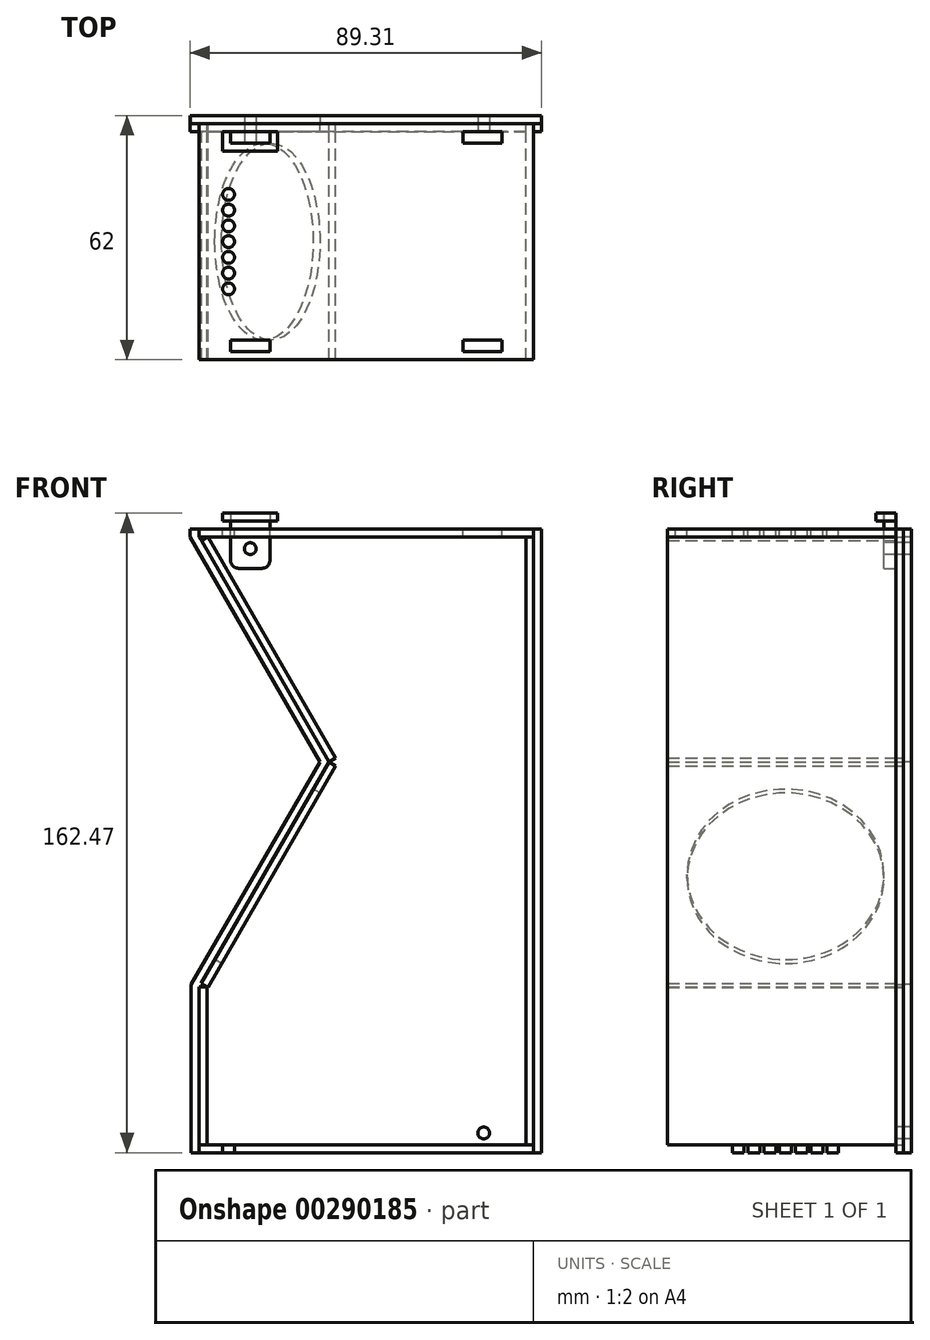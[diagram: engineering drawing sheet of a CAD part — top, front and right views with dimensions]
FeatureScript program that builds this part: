
annotation { "Feature Type Name" : "Feature", "Feature Type Description" : "" }
export const myFeature = defineFeature(function(context is Context, id is Id, definition is map)
    precondition{}
    {
        {
            assignVariable(context, id + "F0", {"name" : "pd", "anyValue" : 2});
        }
        {
            var Q0;
            Q0=qCreatedBy(makeId("Front.planeOp"),FACE);
            var sketch = newSketch(context, id + "F1", { "sketchPlane" : qUnion([Q0])});
            skLineSegment(sketch, "E0", {"start": v(0, 0) * mm, "end": v(25, 43.3) * mm});
            skLineSegment(sketch, "E1", {"start": v(0, 0) * mm, "end": v(43.3, -25) * mm, "construction": true});
            skLineSegment(sketch, "E2", {"start": v(25, 43.3) * mm, "end": v(68.3, 18.3) * mm, "construction": true});
            skLineSegment(sketch, "E3", {"start": v(43.3, -25) * mm, "end": v(68.3, 18.3) * mm, "construction": true});
            skLineSegment(sketch, "E4", {"start": v(0, 0) * mm, "end": v(-4, -6.93) * mm});
            skLineSegment(sketch, "E5", {"start": v(25, 43.3) * mm, "end": v(29, 50.23) * mm});
            skLineSegment(sketch, "E6", {"start": v(-4, 109.39) * mm, "end": v(81, 109.39) * mm});
            skLineSegment(sketch, "E7", {"start": v(81, 107.39) * mm, "end": v(-4, 107.39) * mm});
            skLineSegment(sketch, "E8", {"start": v(-4, 107.39) * mm, "end": v(-4, 109.39) * mm});
            skLineSegment(sketch, "E9", {"start": v(79, 107.39) * mm, "end": v(79, -47.08) * mm});
            skLineSegment(sketch, "E10", {"start": v(81, -49.08) * mm, "end": v(-4, -49.08) * mm});
            skLineSegment(sketch, "E11", {"start": v(-4, -49.08) * mm, "end": v(-4, -47.08) * mm});
            skLineSegment(sketch, "E12", {"start": v(-4, -6.93) * mm, "end": v(-4, -47.08) * mm});
            skLineSegment(sketch, "E13", {"start": v(-4, -6.93) * mm, "end": v(-2, -6.93) * mm});
            skLineSegment(sketch, "E14", {"start": v(-2, -6.93) * mm, "end": v(-2, -47.08) * mm});
            skLineSegment(sketch, "E15", {"start": v(29, 50.23) * mm, "end": v(-4, 107.39) * mm});
            skLineSegment(sketch, "E16", {"start": v(-3.5, -6.06) * mm, "end": v(-1.77, -7.06) * mm});
            skLineSegment(sketch, "E17", {"start": v(29, 50.23) * mm, "end": v(30.73, 49.23) * mm});
            skLineSegment(sketch, "E18", {"start": v(30.73, 49.23) * mm, "end": v(-1.77, -7.06) * mm});
            skLineSegment(sketch, "E19", {"start": v(29, 50.23) * mm, "end": v(30.73, 51.23) * mm});
            skLineSegment(sketch, "E20", {"start": v(30.73, 51.23) * mm, "end": v(-1.7, 107.39) * mm});
            skLineSegment(sketch, "E21", {"start": v(-1.7, 107.39) * mm, "end": v(-3.42, 106.39) * mm});
            skLineSegment(sketch, "E22", {"start": v(81, -49.08) * mm, "end": v(81, 109.39) * mm});
            skLineSegment(sketch, "E23", {"start": v(81, -47.08) * mm, "end": v(-4, -47.08) * mm});
            skSolve(sketch);
        }
        {
            var Q0;
            Q0=sQuery(id+"F1.wireOp",EDGE,"E0");
            cPlane(context, id + "F2", {"entities" : qUnion([Q0]), "cplaneType" : CPlaneType.LINE_ANGLE, "offset" : 25 * mm, "angle" : 0 * degree, "width" : 150 * mm, "height" : 150 * mm});
        }
        {
            var Q0;
            Q0=qCreatedBy(makeId("Front.planeOp"),FACE);
            cPlane(context, id + "F3", {"entities" : qUnion([Q0]), "cplaneType" : CPlaneType.OFFSET, "offset" : 30 * mm, "oppositeDirection" : true, "width" : 150 * mm, "height" : 150 * mm});
        }
        {
            var Q0;
            Q0=qCreatedBy(id+"F2.planeOp",FACE);
            var sketch = newSketch(context, id + "F4", { "sketchPlane" : qUnion([Q0])});
            skLineSegment(sketch, "E24.0", {"start": v(0, 0) * mm, "end": v(0, 50) * mm});
            skCircle(sketch, "E25", {"center": v(0, 25) * mm, "radius": 25 * mm});
            skLineSegment(sketch, "E26.bottom", {"start": v(30, -5) * mm, "end": v(-30, -5) * mm});
            skLineSegment(sketch, "E26.top", {"start": v(30, 55) * mm, "end": v(-30, 55) * mm});
            skLineSegment(sketch, "E26.left", {"start": v(30, -5) * mm, "end": v(30, 55) * mm});
            skLineSegment(sketch, "E26.right", {"start": v(-30, -5) * mm, "end": v(-30, 55) * mm});
            skSolve(sketch);
        }
        {
            var Q0;
            Q0=qCreatedBy(id+"F3.planeOp",FACE);
            var sketch = newSketch(context, id + "F5", { "sketchPlane" : qUnion([Q0])});
            skLineSegment(sketch, "E27.0.0", {"start": v(-2, -47.08) * mm, "end": v(79, -47.08) * mm});
            skLineSegment(sketch, "E27.0.1", {"start": v(79, -47.08) * mm, "end": v(79, 107.39) * mm});
            skLineSegment(sketch, "E27.0.2", {"start": v(79, 107.39) * mm, "end": v(-1.7, 107.39) * mm});
            skLineSegment(sketch, "E27.0.3", {"start": v(-1.7, 107.39) * mm, "end": v(30.73, 51.23) * mm});
            skLineSegment(sketch, "E27.0.4", {"start": v(30.73, 51.23) * mm, "end": v(29, 50.23) * mm});
            skLineSegment(sketch, "E27.0.5", {"start": v(29, 50.23) * mm, "end": v(30.73, 49.23) * mm});
            skLineSegment(sketch, "E27.0.6", {"start": v(30.73, 49.23) * mm, "end": v(-1.77, -7.06) * mm});
            skLineSegment(sketch, "E27.0.7", {"start": v(-1.77, -7.06) * mm, "end": v(-2, -6.93) * mm});
            skLineSegment(sketch, "E27.0.8", {"start": v(-2, -6.93) * mm, "end": v(-2, -47.08) * mm});
            skLineSegment(sketch, "E28.0", {"start": v(-4, 109.39) * mm, "end": v(81, 109.39) * mm});
            skLineSegment(sketch, "E28.1", {"start": v(-4, 107.39) * mm, "end": v(-4, 109.39) * mm});
            skLineSegment(sketch, "E28.2", {"start": v(29, 50.23) * mm, "end": v(-4, 107.39) * mm});
            skLineSegment(sketch, "E28.3", {"start": v(81, -49.08) * mm, "end": v(81, 109.39) * mm});
            skLineSegment(sketch, "E28.4", {"start": v(25, 43.3) * mm, "end": v(29, 50.23) * mm});
            skLineSegment(sketch, "E28.5", {"start": v(0, 0) * mm, "end": v(25, 43.3) * mm});
            skLineSegment(sketch, "E28.6", {"start": v(0, 0) * mm, "end": v(-4, -6.93) * mm});
            skLineSegment(sketch, "E28.7", {"start": v(-4, -6.93) * mm, "end": v(-4, -47.08) * mm});
            skLineSegment(sketch, "E28.8", {"start": v(-4, -49.08) * mm, "end": v(-4, -47.08) * mm});
            skLineSegment(sketch, "E28.9", {"start": v(81, -49.08) * mm, "end": v(-4, -49.08) * mm});
            skLineSegment(sketch, "E29", {"start": v(-4, -49.08) * mm, "end": v(-6, -49.08) * mm});
            skLineSegment(sketch, "E30", {"start": v(-6, -49.08) * mm, "end": v(-6, -6.4) * mm});
            skLineSegment(sketch, "E31", {"start": v(-6, -6.4) * mm, "end": v(26.7, 50.23) * mm});
            skLineSegment(sketch, "E32", {"start": v(26.7, 50.23) * mm, "end": v(-6.3, 107.39) * mm});
            skLineSegment(sketch, "E33", {"start": v(-6.3, 107.39) * mm, "end": v(-6.3, 109.39) * mm});
            skLineSegment(sketch, "E34", {"start": v(-6.3, 109.39) * mm, "end": v(-4, 109.39) * mm});
            skLineSegment(sketch, "E35", {"start": v(81, -49.08) * mm, "end": v(83, -49.08) * mm});
            skLineSegment(sketch, "E36", {"start": v(83, -49.08) * mm, "end": v(83, 109.39) * mm});
            skLineSegment(sketch, "E37", {"start": v(83, 109.39) * mm, "end": v(81, 109.39) * mm});
            skSolve(sketch);
        }
        {
            var Q0;
            Q0=qCreatedBy(id+"F3.planeOp",FACE);
            var sketch = newSketch(context, id + "F6", { "sketchPlane" : qUnion([Q0])});
            skLineSegment(sketch, "E38.0", {"start": v(81, -49.08) * mm, "end": v(-4, -49.08) * mm});
            skLineSegment(sketch, "E38.1", {"start": v(-4, -49.08) * mm, "end": v(-6, -49.08) * mm});
            skLineSegment(sketch, "E38.2", {"start": v(-6, -49.08) * mm, "end": v(-6, -6.4) * mm});
            skLineSegment(sketch, "E38.3", {"start": v(-6, -6.4) * mm, "end": v(26.7, 50.23) * mm});
            skLineSegment(sketch, "E38.4", {"start": v(26.7, 50.23) * mm, "end": v(-6.3, 107.39) * mm});
            skLineSegment(sketch, "E38.5", {"start": v(-6.3, 107.39) * mm, "end": v(-6.3, 109.39) * mm});
            skLineSegment(sketch, "E38.6", {"start": v(-6.3, 109.39) * mm, "end": v(-4, 109.39) * mm});
            skLineSegment(sketch, "E38.7", {"start": v(-4, 109.39) * mm, "end": v(81, 109.39) * mm});
            skLineSegment(sketch, "E38.8", {"start": v(83, -49.08) * mm, "end": v(83, 109.39) * mm});
            skLineSegment(sketch, "E38.9", {"start": v(83, 109.39) * mm, "end": v(81, 109.39) * mm});
            skLineSegment(sketch, "E38.10", {"start": v(81, -49.08) * mm, "end": v(83, -49.08) * mm});
            skSolve(sketch);
        }
        {
            var Q0;
            {var subQ6=sQuery(id+"F1.wireOp",EDGE,"E6");Q0=makeQuery(id+"F1.imprint","IMPRINT",FACE,{"disambiguationData":[TD([[makeQuery(id+"F1.imprint","IMPRINT",EDGE,{"derivedFrom":subQ6}),-1.0]])]});}
            extrude(context, id + "F7", {"entities" : qUnion([Q0]), "depth" : 30 * mm, "hasSecondDirection" : true, "secondDirectionOppositeDirection" : true, "secondDirectionDepth" : 30 * mm});
        }
        {
            var Q0;
            {var subQ3=sQuery(id+"F1.wireOp",EDGE,"E9");Q0=makeQuery(id+"F1.imprint","IMPRINT",FACE,{"disambiguationData":[TD([[makeQuery(id+"F1.imprint","IMPRINT",EDGE,{"derivedFrom":subQ3}),1.0]])]});}
            extrude(context, id + "F8", {"entities" : qUnion([Q0]), "depth" : 30 * mm, "hasSecondDirection" : true, "secondDirectionOppositeDirection" : true, "secondDirectionDepth" : 30 * mm});
        }
        {
            var Q0;
            {var subQ0=sQuery(id+"F1.wireOp",EDGE,"E19");Q0=makeQuery(id+"F1.imprint","IMPRINT",FACE,{"disambiguationData":[TD([[makeQuery(id+"F1.imprint","IMPRINT",EDGE,{"derivedFrom":subQ0}),1.0]])]});}
            extrude(context, id + "F9", {"entities" : qUnion([Q0]), "depth" : 30 * mm, "hasSecondDirection" : true, "secondDirectionOppositeDirection" : true, "secondDirectionDepth" : 30 * mm});
        }
        {
            var Q0;
            {var subQ4=sQuery(id+"F1.wireOp",EDGE,"E0");Q0=makeQuery(id+"F1.imprint","IMPRINT",FACE,{"disambiguationData":[TD([[makeQuery(id+"F1.imprint","IMPRINT",EDGE,{"derivedFrom":subQ4}),-1.0]])]});}
            extrude(context, id + "F10", {"entities" : qUnion([Q0]), "depth" : 30 * mm, "hasSecondDirection" : true, "secondDirectionOppositeDirection" : true, "secondDirectionDepth" : 30 * mm});
        }
        {
            var Q0;
            {var subQ0=sQuery(id+"F1.wireOp",EDGE,"E12");Q0=makeQuery(id+"F1.imprint","IMPRINT",FACE,{"disambiguationData":[TD([[makeQuery(id+"F1.imprint","IMPRINT",EDGE,{"derivedFrom":subQ0}),1.0]])]});}
            extrude(context, id + "F11", {"entities" : qUnion([Q0]), "depth" : 30 * mm, "hasSecondDirection" : true, "secondDirectionOppositeDirection" : true, "secondDirectionDepth" : 30 * mm});
        }
        {
            var Q0;
            {var subQ4=sQuery(id+"F1.wireOp",EDGE,"E10");Q0=makeQuery(id+"F1.imprint","IMPRINT",FACE,{"disambiguationData":[TD([[makeQuery(id+"F1.imprint","IMPRINT",EDGE,{"derivedFrom":subQ4}),-1.0]])]});}
            extrude(context, id + "F12", {"entities" : qUnion([Q0]), "depth" : 30 * mm, "hasSecondDirection" : true, "secondDirectionOppositeDirection" : true, "secondDirectionDepth" : 30 * mm});
        }
        {
            var Q0;
            {var subQ0=sQuery(id+"F4.wireOp",EDGE,"E24.0");Q0=makeQuery(id+"F4.imprint","IMPRINT",FACE,{"disambiguationData":[TD([[makeQuery(id+"F4.imprint","IMPRINT",EDGE,{"derivedFrom":subQ0}),-1.0]])]});}
            var Q1;
            {var subQ0=sQuery(id+"F4.wireOp",EDGE,"E24.0");Q1=makeQuery(id+"F4.imprint","IMPRINT",FACE,{"disambiguationData":[TD([[makeQuery(id+"F4.imprint","IMPRINT",EDGE,{"derivedFrom":subQ0}),1.0]])]});}
            extrude(context, id + "F13", {"entities" : qUnion([Q0, Q1]), "operationType" : NewBodyOperationType.REMOVE, "depth" : 25 * mm});
        }
        {
            var Q0;
            Q0=makeQuery(id+"F7.opExtrude","SWEPT_FACE",FACE,{"disambiguationData":[OSD([sQuery(id+"F1.wireOp",EDGE,"E6")])]});
            var sketch = newSketch(context, id + "F14", { "sketchPlane" : qUnion([Q0])});
            skLineSegment(sketch, "E39", {"start": v(3.5, 30) * mm, "end": v(3.5, -30) * mm, "construction": true});
            skCircle(sketch, "E40", {"center": v(3.5, -12) * mm, "radius": 1.5 * mm});
            skCircle(sketch, "E41.0.1.0", {"center": v(3.5, -8) * mm, "radius": 1.5 * mm});
            skCircle(sketch, "E41.0.2.0", {"center": v(3.5, -4) * mm, "radius": 1.5 * mm});
            skCircle(sketch, "E41.0.3.0", {"center": v(3.5, 0) * mm, "radius": 1.5 * mm});
            skCircle(sketch, "E41.0.4.0", {"center": v(3.5, 4) * mm, "radius": 1.5 * mm});
            skCircle(sketch, "E41.0.5.0", {"center": v(3.5, 8) * mm, "radius": 1.5 * mm});
            skCircle(sketch, "E41.0.6.0", {"center": v(3.5, 12) * mm, "radius": 1.5 * mm});
            skLineSegment(sketch, "E41.direction1", {"start": v(3.5, -12) * mm, "end": v(64.86, -12) * mm, "construction": true});
            skLineSegment(sketch, "E41.direction2", {"start": v(3.5, -12) * mm, "end": v(3.5, -8) * mm, "construction": true});
            skLineSegment(sketch, "E42.bottom", {"start": v(14, 28) * mm, "end": v(4, 28) * mm});
            skLineSegment(sketch, "E42.top", {"start": v(14, 25) * mm, "end": v(4, 25) * mm});
            skLineSegment(sketch, "E42.left", {"start": v(14, 25) * mm, "end": v(14, 28) * mm});
            skLineSegment(sketch, "E42.right", {"start": v(4, 25) * mm, "end": v(4, 28) * mm});
            skPoint(sketch, "E42.middle", {"position": v(9, 26.5) * mm});
            skLineSegment(sketch, "E43", {"start": v(38.5, -30) * mm, "end": v(38.5, 30) * mm, "construction": true});
            skLineSegment(sketch, "E44.MirrorCS", {"start": v(63, 25) * mm, "end": v(73, 25) * mm});
            skLineSegment(sketch, "E45.MirrorCS", {"start": v(63, 28) * mm, "end": v(73, 28) * mm});
            skLineSegment(sketch, "E46.MirrorCS", {"start": v(73, 25) * mm, "end": v(73, 28) * mm});
            skLineSegment(sketch, "E47.MirrorCS", {"start": v(63, 25) * mm, "end": v(63, 28) * mm});
            skLineSegment(sketch, "E48.MirrorCS", {"start": v(14, -25) * mm, "end": v(4, -25) * mm});
            skLineSegment(sketch, "E49.MirrorCS", {"start": v(14, -25) * mm, "end": v(14, -28) * mm});
            skLineSegment(sketch, "E50.MirrorCS", {"start": v(14, -28) * mm, "end": v(4, -28) * mm});
            skLineSegment(sketch, "E51.MirrorCS", {"start": v(4, -25) * mm, "end": v(4, -28) * mm});
            skLineSegment(sketch, "E52.MirrorCS", {"start": v(63, -25) * mm, "end": v(63, -28) * mm});
            skLineSegment(sketch, "E53.MirrorCS", {"start": v(63, -28) * mm, "end": v(73, -28) * mm});
            skLineSegment(sketch, "E54.MirrorCS", {"start": v(73, -25) * mm, "end": v(73, -28) * mm});
            skLineSegment(sketch, "E55.MirrorCS", {"start": v(63, -25) * mm, "end": v(73, -25) * mm});
            skSolve(sketch);
        }
        {
            var Q0;
            Q0=makeQuery(id+"F14.imprint","IMPRINT",FACE,{"disambiguationData":[TD([[makeQuery(id+"F14.imprint","IMPRINT",EDGE,{"derivedFrom":sQuery(id+"F14.wireOp",EDGE,"E41.0.8.0")}),1.0]])]});
            var Q1;
            Q1=makeQuery(id+"F14.imprint","IMPRINT",FACE,{"disambiguationData":[TD([[makeQuery(id+"F14.imprint","IMPRINT",EDGE,{"derivedFrom":sQuery(id+"F14.wireOp",EDGE,"E41.0.7.0")}),1.0]])]});
            var Q2;
            Q2=makeQuery(id+"F14.imprint","IMPRINT",FACE,{"disambiguationData":[TD([[makeQuery(id+"F14.imprint","IMPRINT",EDGE,{"derivedFrom":sQuery(id+"F14.wireOp",EDGE,"E41.0.6.0")}),1.0]])]});
            var Q3;
            Q3=makeQuery(id+"F14.imprint","IMPRINT",FACE,{"disambiguationData":[TD([[makeQuery(id+"F14.imprint","IMPRINT",EDGE,{"derivedFrom":sQuery(id+"F14.wireOp",EDGE,"E41.0.5.0")}),1.0]])]});
            var Q4;
            Q4=makeQuery(id+"F14.imprint","IMPRINT",FACE,{"disambiguationData":[TD([[makeQuery(id+"F14.imprint","IMPRINT",EDGE,{"derivedFrom":sQuery(id+"F14.wireOp",EDGE,"E41.0.4.0")}),1.0]])]});
            var Q5;
            Q5=makeQuery(id+"F14.imprint","IMPRINT",FACE,{"disambiguationData":[TD([[makeQuery(id+"F14.imprint","IMPRINT",EDGE,{"derivedFrom":sQuery(id+"F14.wireOp",EDGE,"E41.0.2.0")}),1.0]])]});
            var Q6;
            Q6=makeQuery(id+"F14.imprint","IMPRINT",FACE,{"disambiguationData":[TD([[makeQuery(id+"F14.imprint","IMPRINT",EDGE,{"derivedFrom":sQuery(id+"F14.wireOp",EDGE,"E41.0.3.0")}),1.0]])]});
            var Q7;
            Q7=makeQuery(id+"F14.imprint","IMPRINT",FACE,{"disambiguationData":[TD([[makeQuery(id+"F14.imprint","IMPRINT",EDGE,{"derivedFrom":sQuery(id+"F14.wireOp",EDGE,"E41.0.1.0")}),1.0]])]});
            var Q8;
            Q8=makeQuery(id+"F14.imprint","IMPRINT",FACE,{"disambiguationData":[TD([[makeQuery(id+"F14.imprint","IMPRINT",EDGE,{"derivedFrom":sQuery(id+"F14.wireOp",EDGE,"E40")}),1.0]])]});
            var Q9;
            Q9=makeQuery(id+"F14.imprint","IMPRINT",FACE,{"disambiguationData":[TD([[makeQuery(id+"F14.imprint","IMPRINT",EDGE,{"derivedFrom":sQuery(id+"F14.wireOp",EDGE,"E42.bottom")}),1.0]])]});
            var Q10;
            Q10=makeQuery(id+"F14.imprint","IMPRINT",FACE,{"disambiguationData":[TD([[makeQuery(id+"F14.imprint","IMPRINT",EDGE,{"derivedFrom":sQuery(id+"F14.wireOp",EDGE,"E44.MirrorCS")}),1.0]])]});
            var Q11;
            Q11=makeQuery(id+"F14.imprint","IMPRINT",FACE,{"disambiguationData":[TD([[makeQuery(id+"F14.imprint","IMPRINT",EDGE,{"derivedFrom":sQuery(id+"F14.wireOp",EDGE,"E52.MirrorCS")}),1.0]])]});
            var Q12;
            Q12=makeQuery(id+"F14.imprint","IMPRINT",FACE,{"disambiguationData":[TD([[makeQuery(id+"F14.imprint","IMPRINT",EDGE,{"derivedFrom":sQuery(id+"F14.wireOp",EDGE,"E48.MirrorCS")}),1.0]])]});
            extrude(context, id + "F15", {"entities" : qUnion([Q0, Q1, Q2, Q3, Q4, Q5, Q6, Q7, Q8, Q9, Q10, Q11, Q12]), "operationType" : NewBodyOperationType.REMOVE, "oppositeDirection" : true, "depth" : (getVariable(context, 'pd')) * mm});
        }
        {
            var Q0;
            Q0=makeQuery(id+"F12.opExtrude","SWEPT_FACE",FACE,{"disambiguationData":[OSD([sQuery(id+"F1.wireOp",EDGE,"E10")])]});
            var sketch = newSketch(context, id + "F16", { "sketchPlane" : qUnion([Q0])});
            skLineSegment(sketch, "E56.0", {"start": v(14, 25) * mm, "end": v(4, 25) * mm});
            skLineSegment(sketch, "E56.1", {"start": v(14, 28) * mm, "end": v(4, 28) * mm});
            skLineSegment(sketch, "E56.2", {"start": v(14, 25) * mm, "end": v(14, 28) * mm});
            skLineSegment(sketch, "E56.3", {"start": v(4, 25) * mm, "end": v(4, 28) * mm});
            skCircle(sketch, "E56.4", {"center": v(3.5, 12) * mm, "radius": 1.5 * mm});
            skCircle(sketch, "E56.5", {"center": v(3.5, 8) * mm, "radius": 1.5 * mm});
            skCircle(sketch, "E56.6", {"center": v(3.5, 4) * mm, "radius": 1.5 * mm});
            skCircle(sketch, "E56.7", {"center": v(3.5, 0) * mm, "radius": 1.5 * mm});
            skCircle(sketch, "E56.8", {"center": v(3.5, -4) * mm, "radius": 1.5 * mm});
            skCircle(sketch, "E56.9", {"center": v(3.5, -8) * mm, "radius": 1.5 * mm});
            skCircle(sketch, "E56.10", {"center": v(3.5, -12) * mm, "radius": 1.5 * mm});
            skLineSegment(sketch, "E56.11", {"start": v(14, -25) * mm, "end": v(4, -25) * mm});
            skLineSegment(sketch, "E56.12", {"start": v(14, -28) * mm, "end": v(4, -28) * mm});
            skLineSegment(sketch, "E56.13", {"start": v(14, -25) * mm, "end": v(14, -28) * mm});
            skLineSegment(sketch, "E56.14", {"start": v(4, -25) * mm, "end": v(4, -28) * mm});
            skLineSegment(sketch, "E56.15", {"start": v(63, -25) * mm, "end": v(73, -25) * mm});
            skLineSegment(sketch, "E56.16", {"start": v(63, -28) * mm, "end": v(73, -28) * mm});
            skLineSegment(sketch, "E56.17", {"start": v(73, -25) * mm, "end": v(73, -28) * mm});
            skLineSegment(sketch, "E56.18", {"start": v(63, -25) * mm, "end": v(63, -28) * mm});
            skLineSegment(sketch, "E56.19", {"start": v(63, 25) * mm, "end": v(73, 25) * mm});
            skLineSegment(sketch, "E56.20", {"start": v(63, 25) * mm, "end": v(63, 28) * mm});
            skLineSegment(sketch, "E56.21", {"start": v(63, 28) * mm, "end": v(73, 28) * mm});
            skLineSegment(sketch, "E56.22", {"start": v(73, 25) * mm, "end": v(73, 28) * mm});
            skSolve(sketch);
        }
        {
            var Q0;
            Q0=makeQuery(id+"F16.imprint","IMPRINT",FACE,{"disambiguationData":[TD([[makeQuery(id+"F16.imprint","IMPRINT",EDGE,{"derivedFrom":sQuery(id+"F16.wireOp",EDGE,"E56.11")}),1.0]])]});
            var Q1;
            Q1=makeQuery(id+"F16.imprint","IMPRINT",FACE,{"disambiguationData":[TD([[makeQuery(id+"F16.imprint","IMPRINT",EDGE,{"derivedFrom":sQuery(id+"F16.wireOp",EDGE,"E56.10")}),-1.0]])]});
            var Q2;
            Q2=makeQuery(id+"F16.imprint","IMPRINT",FACE,{"disambiguationData":[TD([[makeQuery(id+"F16.imprint","IMPRINT",EDGE,{"derivedFrom":sQuery(id+"F16.wireOp",EDGE,"E56.9")}),-1.0]])]});
            var Q3;
            Q3=makeQuery(id+"F16.imprint","IMPRINT",FACE,{"disambiguationData":[TD([[makeQuery(id+"F16.imprint","IMPRINT",EDGE,{"derivedFrom":sQuery(id+"F16.wireOp",EDGE,"E56.8")}),-1.0]])]});
            var Q4;
            Q4=makeQuery(id+"F16.imprint","IMPRINT",FACE,{"disambiguationData":[TD([[makeQuery(id+"F16.imprint","IMPRINT",EDGE,{"derivedFrom":sQuery(id+"F16.wireOp",EDGE,"E56.7")}),-1.0]])]});
            var Q5;
            Q5=makeQuery(id+"F16.imprint","IMPRINT",FACE,{"disambiguationData":[TD([[makeQuery(id+"F16.imprint","IMPRINT",EDGE,{"derivedFrom":sQuery(id+"F16.wireOp",EDGE,"E56.6")}),-1.0]])]});
            var Q6;
            Q6=makeQuery(id+"F16.imprint","IMPRINT",FACE,{"disambiguationData":[TD([[makeQuery(id+"F16.imprint","IMPRINT",EDGE,{"derivedFrom":sQuery(id+"F16.wireOp",EDGE,"E56.5")}),-1.0]])]});
            var Q7;
            Q7=makeQuery(id+"F16.imprint","IMPRINT",FACE,{"disambiguationData":[TD([[makeQuery(id+"F16.imprint","IMPRINT",EDGE,{"derivedFrom":sQuery(id+"F16.wireOp",EDGE,"E56.4")}),-1.0]])]});
            var Q8;
            Q8=makeQuery(id+"F16.imprint","IMPRINT",FACE,{"disambiguationData":[TD([[makeQuery(id+"F16.imprint","IMPRINT",EDGE,{"derivedFrom":sQuery(id+"F16.wireOp",EDGE,"E56.0")}),-1.0]])]});
            var Q9;
            Q9=makeQuery(id+"F16.imprint","IMPRINT",FACE,{"disambiguationData":[TD([[makeQuery(id+"F16.imprint","IMPRINT",EDGE,{"derivedFrom":sQuery(id+"F16.wireOp",EDGE,"E56.19")}),1.0]])]});
            var Q10;
            Q10=makeQuery(id+"F16.imprint","IMPRINT",FACE,{"disambiguationData":[TD([[makeQuery(id+"F16.imprint","IMPRINT",EDGE,{"derivedFrom":sQuery(id+"F16.wireOp",EDGE,"E56.15")}),-1.0]])]});
            extrude(context, id + "F17", {"entities" : qUnion([Q0, Q1, Q2, Q3, Q4, Q5, Q6, Q7, Q8, Q9, Q10]), "operationType" : NewBodyOperationType.REMOVE, "oppositeDirection" : true, "depth" : (getVariable(context, 'pd')) * mm});
        }
        {
            var Q0;
            Q0=makeQuery(id+"F5.imprint","IMPRINT",FACE,{"disambiguationData":[TD([[makeQuery(id+"F5.imprint","IMPRINT",EDGE,{"derivedFrom":sQuery(id+"F5.wireOp",EDGE,"E27.0.0")}),1.0]])]});
            extrude(context, id + "F18", {"entities" : qUnion([Q0]), "depth" : (getVariable(context, 'pd')) * mm});
        }
        {
            var Q0;
            Q0=makeQuery(id+"F5.imprint","IMPRINT",FACE,{"disambiguationData":[TD([[makeQuery(id+"F5.imprint","IMPRINT",EDGE,{"derivedFrom":sQuery(id+"F5.wireOp",EDGE,"E28.3")}),-1.0]])]});
            var Q1;
            Q1=makeQuery(id+"F5.imprint","IMPRINT",FACE,{"disambiguationData":[TD([[makeQuery(id+"F5.imprint","IMPRINT",EDGE,{"derivedFrom":sQuery(id+"F5.wireOp",EDGE,"E28.1")}),1.0]])]});
            extrude(context, id + "F19", {"entities" : qUnion([Q0, Q1]), "depth" : (getVariable(context, 'pd')) * mm});
        }
        {
            var Q0;
            Q0=makeQuery(id+"F6.imprint","IMPRINT",FACE,{"disambiguationData":[TD([[makeQuery(id+"F6.imprint","IMPRINT",EDGE,{"derivedFrom":sQuery(id+"F6.wireOp",EDGE,"E38.0")}),-1.0]])]});
            extrude(context, id + "F20", {"entities" : qUnion([Q0]), "oppositeDirection" : true, "depth" : (getVariable(context, 'pd')) * mm});
        }
        {
            var Q0;
            Q0=makeQuery(id+"F14.imprint","IMPRINT",FACE,{"disambiguationData":[TD([[makeQuery(id+"F14.imprint","IMPRINT",EDGE,{"derivedFrom":sQuery(id+"F14.wireOp",EDGE,"E40")}),-1.0]])]});
            cPlane(context, id + "F21", {"entities" : qUnion([Q0]), "cplaneType" : CPlaneType.OFFSET, "offset" : (getVariable(context, 'pd')) * mm, "width" : 150 * mm, "height" : 150 * mm});
        }
        {
            var Q0;
            Q0=qCreatedBy(id+"F21.planeOp",FACE);
            var sketch = newSketch(context, id + "F22", { "sketchPlane" : qUnion([Q0])});
            skLineSegment(sketch, "E57.0", {"start": v(14, 25) * mm, "end": v(4, 25) * mm});
            skLineSegment(sketch, "E57.1", {"start": v(14, 25) * mm, "end": v(14, 28) * mm});
            skLineSegment(sketch, "E57.2", {"start": v(14, 28) * mm, "end": v(4, 28) * mm});
            skLineSegment(sketch, "E57.3", {"start": v(4, 25) * mm, "end": v(4, 28) * mm});
            skLineSegment(sketch, "E58", {"start": v(4, 28) * mm, "end": v(2, 28) * mm});
            skLineSegment(sketch, "E59", {"start": v(2, 28) * mm, "end": v(2, 23) * mm});
            skLineSegment(sketch, "E60", {"start": v(2, 23) * mm, "end": v(16, 23) * mm});
            skLineSegment(sketch, "E61", {"start": v(16, 23) * mm, "end": v(16, 28) * mm});
            skLineSegment(sketch, "E62", {"start": v(16, 28) * mm, "end": v(14, 28) * mm});
            skSolve(sketch);
        }
        {
            var Q0;
            Q0=makeQuery(id+"F22.imprint","IMPRINT",FACE,{"disambiguationData":[TD([[makeQuery(id+"F22.imprint","IMPRINT",EDGE,{"derivedFrom":sQuery(id+"F22.wireOp",EDGE,"E57.0")}),-1.0]])]});
            extrude(context, id + "F23", {"entities" : qUnion([Q0]), "oppositeDirection" : true, "depth" : 12 * mm, "hasSecondDirection" : true, "secondDirectionOppositeDirection" : false, "secondDirectionDepth" : (getVariable(context, 'pd')) * mm});
        }
        {
            var Q0;
            Q0=makeQuery(id+"F22.imprint","IMPRINT",FACE,{"disambiguationData":[TD([[makeQuery(id+"F22.imprint","IMPRINT",EDGE,{"derivedFrom":sQuery(id+"F22.wireOp",EDGE,"E57.0")}),1.0]])]});
            extrude(context, id + "F24", {"entities" : qUnion([Q0]), "depth" : (getVariable(context, 'pd')) * mm});
        }
        {
            var Q0;
            Q0=makeQuery(id+"F23.opExtrude","CAP_EDGE",EDGE,{"disambiguationData":[OSD([sQuery(id+"F22.wireOp",EDGE,"E57.1")])],"isStart":false});
            var Q1;
            Q1=makeQuery(id+"F23.opExtrude","CAP_EDGE",EDGE,{"disambiguationData":[OSD([sQuery(id+"F22.wireOp",EDGE,"E57.3")])],"isStart":false});
            fillet(context, id + "F25", {"entities" : qUnion([Q0, Q1]), "radius" : 2 * mm, "tangentPropagation" : true, "allowEdgeOverflow" : false});
        }
        {
            var Q0;
            Q0=makeQuery(id+"F23.opExtrude","SWEPT_FACE",FACE,{"disambiguationData":[OSD([sQuery(id+"F22.wireOp",EDGE,"E57.0")])]});
            var sketch = newSketch(context, id + "F26", { "sketchPlane" : qUnion([Q0])});
            skLineSegment(sketch, "E63.0", {"start": v(4, 101.39) * mm, "end": v(4, 113.39) * mm});
            skLineSegment(sketch, "E64.0", {"start": v(14, 107.39) * mm, "end": v(4, 107.39) * mm});
            skLineSegment(sketch, "E65.0", {"start": v(14, 101.39) * mm, "end": v(14, 113.39) * mm});
            skLineSegment(sketch, "E66", {"start": v(4, 107.39) * mm, "end": v(14, 101.39) * mm, "construction": true});
            skCircle(sketch, "E67", {"center": v(9, 104.39) * mm, "radius": 1.5 * mm});
            skLineSegment(sketch, "E68.0", {"start": v(79, 107.39) * mm, "end": v(-1.7, 107.39) * mm});
            skLineSegment(sketch, "E69", {"start": v(38.65, 107.39) * mm, "end": v(38.65, 89.08) * mm, "construction": true});
            skCircle(sketch, "E70.MirrorC", {"center": v(68.3, 104.39) * mm, "radius": 1.5 * mm});
            skLineSegment(sketch, "E71.0", {"start": v(79, -47.08) * mm, "end": v(79, 107.39) * mm});
            skLineSegment(sketch, "E72", {"start": v(79, 30.16) * mm, "end": v(27.65, 30.16) * mm, "construction": true});
            skPoint(sketch, "E72.endSnap0", {"position": v(79, 30.16) * mm});
            skCircle(sketch, "E73.MirrorC", {"center": v(9, -44.08) * mm, "radius": 1.5 * mm});
            skCircle(sketch, "E74.MirrorC", {"center": v(68.3, -44.08) * mm, "radius": 1.5 * mm});
            skSolve(sketch);
        }
        {
            var Q0;
            Q0=makeQuery(id+"F26.imprint","IMPRINT",FACE,{"disambiguationData":[TD([[makeQuery(id+"F26.imprint","IMPRINT",EDGE,{"derivedFrom":sQuery(id+"F26.wireOp",EDGE,"E67")}),1.0]])]});
            var Q1;
            Q1=makeQuery(id+"F26.imprint","IMPRINT",FACE,{"disambiguationData":[TD([[makeQuery(id+"F26.imprint","IMPRINT",EDGE,{"derivedFrom":sQuery(id+"F26.wireOp",EDGE,"E70.MirrorC")}),-1.0]])]});
            var Q2;
            Q2=makeQuery(id+"F26.imprint","IMPRINT",FACE,{"disambiguationData":[TD([[makeQuery(id+"F26.imprint","IMPRINT",EDGE,{"derivedFrom":sQuery(id+"F26.wireOp",EDGE,"E73.MirrorC")}),-1.0]])]});
            var Q3;
            Q3=makeQuery(id+"F26.imprint","IMPRINT",FACE,{"disambiguationData":[TD([[makeQuery(id+"F26.imprint","IMPRINT",EDGE,{"derivedFrom":sQuery(id+"F26.wireOp",EDGE,"E74.MirrorC")}),1.0]])]});
            extrude(context, id + "F27", {"entities" : qUnion([Q0, Q1, Q2, Q3]), "operationType" : NewBodyOperationType.REMOVE, "oppositeDirection" : true, "depth" : 50 * mm});
        }
    });
